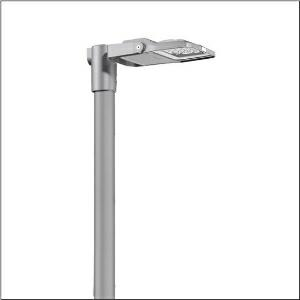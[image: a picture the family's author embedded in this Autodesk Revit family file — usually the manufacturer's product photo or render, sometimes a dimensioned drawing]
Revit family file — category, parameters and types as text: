
# Revit family: floodlight_fl_21_iq_micro___pl61_5xa7762a4c3a_196d
name_source: partatom
category: Lighting Fixtures
units: mm (PartAtom-declared; Revit-internal decimal feet)

## family parameters
Cut with Voids When Loaded = No
Host = Face
Light Source = No
Part Type = Normal
Room Calculation Point = No
Round Connector Dimension = Use Diameter
Shared = No

## types (1)
- --- (1 x LED, 3030 lm, 23.1 W, 4000K)
    Apparent Load = 23 VA
    CIE Flux Codes = 33 65 98 100 100
    Color Rendering = 70
    Color Temperature = 4000K
    Default Elevation = 1800 mm
    Description = Floodlight FL 21 iQ micro, floodlight, primary light control with lens, of PMMA, primary optical cover: protective disc, of toughened safety glass, transparent, light distribution: PL61, light emission: direct distribution, installation type: surface-mounted, LED, High Power LED, rated luminous flux: 3.030lm, luminous efficacy: 131lm/W, light colour: 740, colour temperature: 4000K, control gear: iQ Street-Remote/DALI, control: Auto-Match, Temp-Guard, Night-Set, Smart-Wire, Desk-Remote (wireless, voltage-free reading and setting of iQ features in the workshop via application-optimized NFC function/RFID function), optimised constant luminous flux control (CLO 2.0), Street-Remote, with terminal, 6-pole, mains connection: 220..240V, AC, 50/60Hz, start of lifetime: 23W, end of service life: 24W, reduction: 11W, luminaire housing, of diecast aluminium, powder-coated, Siteco® metallic grey (DB 702S), corrosivity category C5 mid according to DIN EN ISO 12944, suitable for swimming pools, chlorine-resistant, sealing non-destructively replaceable, please order mast flange separately, mast bracket, of steel, galvanised, powder-coated, Siteco® metallic grey (DB 702S), protection rating (complete): IP66, insulation class (complete): insulation class II (safety insulation), certification: CE, ENEC, VDE, protection symbol: D, impact resistance: IK07, permissible operating ambient temperature: -40..+40°C, permissible operating ambient temperature for outdoor applications: -40..+50°C, standard: DIN EN 12944, LABS conformity tested according to VDMA 24364:2018-05, packaging unit: 1 piece

Light Distribution: PL61
    Height = 65 mm
    Lamp = 1 x LED
    Lamp Light Flux = 3030 lm
    Lamp Power = 23.1 W
    Lamp count = 1
    Length = 312 mm
    Luminous efficacy = 131 lm/W
    Manufacturer = Siteco
    ModVariant = No
    Model = 5XA7762A4C3A
    Number of Poles = 1
    OnlyDefault = Yes
    Power Factor = 1
    Product Name = Floodlight FL 21 iQ micro | PL61
    Product group = floodlight | pylon annexe
    ProductGroupID = 6200
    Protection Class = Protection class II
    Protection Degree = IP 66
    RLX_Detail_Level = 1
    RLX_Emergency_Light_Flux = 0 lm
    RLX_Emergency_Type = 0
    RLX_Emergency_Type_DB = No
    RlxData = <blob elided: 102125 chars, md5=d2a9ecb4>
    Socket = socket
    Standby Power = 0 W
    System Light Flux = 3030 lm
    System Power = 23 W
    Type Comments = factory setting: luminous flux: 100 % | dim-lin: 254 | 455 mA
    Type Image = l_1007121.jpg
    URL = http://relux.com
    VarID = @adj_194260
    Voltage = 0 V
    Weight = 0.00 kg
    Width = 230 mm

## geometry (parser evidence)
native form markers: Blend x4, Sweep x9
no freeform markers — native parametric forms only
